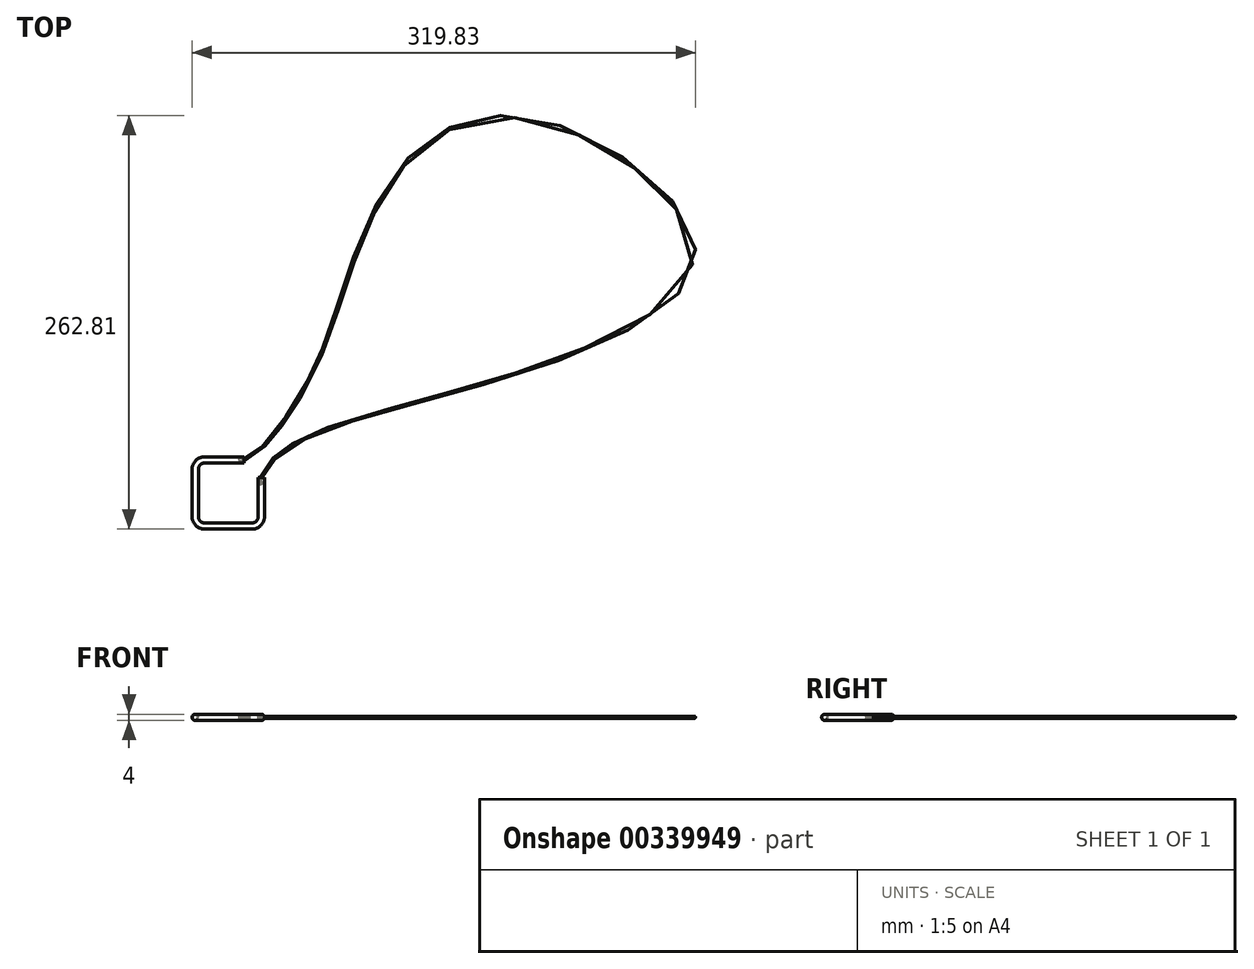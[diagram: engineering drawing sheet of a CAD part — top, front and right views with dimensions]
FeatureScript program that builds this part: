
annotation { "Feature Type Name" : "Feature", "Feature Type Description" : "" }
export const myFeature = defineFeature(function(context is Context, id is Id, definition is map)
    precondition{}
    {
        {
            var Q0;
            Q0=qCreatedBy(makeId("Top.planeOp"),FACE);
            var sketch = newSketch(context, id + "F0", { "sketchPlane" : qUnion([Q0])});
            skLineSegment(sketch, "E0.bottom", {"start": v(-23, 23) * mm, "end": v(23, 23) * mm});
            skLineSegment(sketch, "E0.top", {"start": v(-23, -23) * mm, "end": v(23, -23) * mm});
            skLineSegment(sketch, "E0.left", {"start": v(-23, 23) * mm, "end": v(-23, -23) * mm});
            skLineSegment(sketch, "E0.right", {"start": v(23, 23) * mm, "end": v(23, -23) * mm});
            skPoint(sketch, "E0.middle", {"position": v(0, 0) * mm});
            skSolve(sketch);
        }
        {
            var Q0;
            Q0 = qSketchRegion(id + "F0", true);
            extrude(context, id + "F1", {"entities" : qUnion([Q0]), "depth" : 2 * mm, "offsetDistance" : 25 * mm, "hasSecondDirection" : true, "secondDirectionOppositeDirection" : true, "secondDirectionDepth" : 2 * mm});
        }
        {
            var Q0;
            Q0=makeQuery(id+"F1.opExtrude","SWEPT_EDGE",EDGE,{"disambiguationData":[OSD([sQuery(id+"F0.wireOp",EDGE,"E0.bottom"),sQuery(id+"F0.wireOp",EDGE,"E0.left")])]});
            var Q1;
            Q1=makeQuery(id+"F1.opExtrude","SWEPT_EDGE",EDGE,{"disambiguationData":[OSD([sQuery(id+"F0.wireOp",EDGE,"E0.top"),sQuery(id+"F0.wireOp",EDGE,"E0.left")])]});
            var Q2;
            Q2=makeQuery(id+"F1.opExtrude","SWEPT_EDGE",EDGE,{"disambiguationData":[OSD([sQuery(id+"F0.wireOp",EDGE,"E0.top"),sQuery(id+"F0.wireOp",EDGE,"E0.right")])]});
            var Q3;
            Q3=makeQuery(id+"F1.opExtrude","SWEPT_EDGE",EDGE,{"disambiguationData":[OSD([sQuery(id+"F0.wireOp",EDGE,"E0.bottom"),sQuery(id+"F0.wireOp",EDGE,"E0.right")])]});
            fillet(context, id + "F2", {"entities" : qUnion([Q0, Q1, Q2, Q3]), "radius" : 8 * mm, "tangentPropagation" : true, "allowEdgeOverflow" : false});
        }
        {
            var Q0;
            Q0=makeQuery(id+"F1.opExtrude","CAP_FACE",FACE,{"disambiguationData":[OSD([sQuery(id+"F0.wireOp",EDGE,"E0.bottom"),sQuery(id+"F0.wireOp",EDGE,"E0.top"),sQuery(id+"F0.wireOp",EDGE,"E0.left"),sQuery(id+"F0.wireOp",EDGE,"E0.right")])],"isStart":false});
            var sketch = newSketch(context, id + "F3", { "sketchPlane" : qUnion([Q0])});
            skArc(sketch, "E1.0", {"start": v(-15, 19) * mm, "mid": v(-17.83, 17.83) * mm, "end": v(-19, 15) * mm});
            skLineSegment(sketch, "E1.1", {"start": v(15, 19) * mm, "end": v(-15, 19) * mm});
            skLineSegment(sketch, "E1.2", {"start": v(-19, 15) * mm, "end": v(-19, -15) * mm});
            skArc(sketch, "E1.3", {"start": v(19, 15) * mm, "mid": v(17.83, 17.83) * mm, "end": v(15, 19) * mm});
            skArc(sketch, "E1.4", {"start": v(-19, -15) * mm, "mid": v(-17.83, -17.83) * mm, "end": v(-15, -19) * mm});
            skLineSegment(sketch, "E1.5", {"start": v(-15, -19) * mm, "end": v(15, -19) * mm});
            skArc(sketch, "E1.6", {"start": v(15, -19) * mm, "mid": v(17.83, -17.83) * mm, "end": v(19, -15) * mm});
            skLineSegment(sketch, "E1.7", {"start": v(19, -15) * mm, "end": v(19, 15) * mm});
            skSolve(sketch);
        }
        {
            var Q0;
            Q0 = qSketchRegion(id + "F3", true);
            extrude(context, id + "F4", {"entities" : qUnion([Q0]), "operationType" : NewBodyOperationType.REMOVE, "oppositeDirection" : true, "depth" : 25 * mm, "offsetDistance" : 25 * mm});
        }
        {
            var Q0;
            Q0=makeQuery(id+"F1.opExtrude","CAP_FACE",FACE,{"disambiguationData":[OSD([sQuery(id+"F0.wireOp",EDGE,"E0.bottom"),sQuery(id+"F0.wireOp",EDGE,"E0.top"),sQuery(id+"F0.wireOp",EDGE,"E0.left"),sQuery(id+"F0.wireOp",EDGE,"E0.right")])],"isStart":false});
            var sketch = newSketch(context, id + "F5", { "sketchPlane" : qUnion([Q0])});
            skLineSegment(sketch, "E2", {"start": v(10, 23) * mm, "end": v(10, 19) * mm});
            skLineSegment(sketch, "E3", {"start": v(19, 10) * mm, "end": v(23, 10) * mm});
            skSolve(sketch);
        }
        {
            var Q0;
            {var subQ5=sQuery(id+"F5.wireOp",EDGE,"E2");Q0=makeQuery(id+"F5.imprint","IMPRINT",FACE,{"disambiguationData":[TD([[makeQuery(id+"F5.imprint","IMPRINT",EDGE,{"derivedFrom":subQ5}),1.0]])]});}
            extrude(context, id + "F6", {"entities" : qUnion([Q0]), "operationType" : NewBodyOperationType.REMOVE, "oppositeDirection" : true, "depth" : 25 * mm, "offsetDistance" : 25 * mm});
        }
        {
            var Q0;
            Q0=makeQuery(id+"F4.boolean.opBoolean","INTERSECT",EDGE,{"derivedFrom":[makeQuery(id+"F1.opExtrude","CAP_FACE",FACE,{"disambiguationData":[OSD([sQuery(id+"F0.wireOp",EDGE,"E0.bottom"),sQuery(id+"F0.wireOp",EDGE,"E0.top"),sQuery(id+"F0.wireOp",EDGE,"E0.left"),sQuery(id+"F0.wireOp",EDGE,"E0.right")])],"isStart":true}),makeQuery(id+"F4.opExtrude","SWEPT_FACE",FACE,{"disambiguationData":[OSD([sQuery(id+"F3.wireOp",EDGE,"E1.1")])]})]});
            var Q1;
            Q1=makeQuery(id+"F1.opExtrude","CAP_EDGE",EDGE,{"disambiguationData":[OSD([sQuery(id+"F0.wireOp",EDGE,"E0.bottom")])],"isStart":false});
            var Q2;
            Q2=makeQuery(id+"F4.boolean.opBoolean","COPY",EDGE,{"derivedFrom":makeQuery(id+"F4.opExtrude","CAP_EDGE",EDGE,{"disambiguationData":[OSD([sQuery(id+"F3.wireOp",EDGE,"E1.1")])],"isStart":true})});
            var Q3;
            Q3=makeQuery(id+"F1.opExtrude","CAP_EDGE",EDGE,{"disambiguationData":[OSD([sQuery(id+"F0.wireOp",EDGE,"E0.bottom")])],"isStart":true});
            fillet(context, id + "F7", {"entities" : qUnion([Q0, Q1, Q2, Q3]), "radius" : 2 * mm, "tangentPropagation" : true, "allowEdgeOverflow" : false});
        }
        {
            var Q0;
            Q0=makeQuery(id+"F6.boolean.opBoolean","COPY",FACE,{"derivedFrom":makeQuery(id+"F6.opExtrude","SWEPT_FACE",FACE,{"disambiguationData":[OSD([sQuery(id+"F5.wireOp",EDGE,"E3")])]})});
            var Q1;
            Q1=makeQuery(id+"F6.boolean.opBoolean","COPY",FACE,{"derivedFrom":makeQuery(id+"F6.opExtrude","SWEPT_FACE",FACE,{"disambiguationData":[OSD([sQuery(id+"F5.wireOp",EDGE,"E2")])]})});
            shell(context, id + "F8", {"entities" : qUnion([Q0, Q1]), "thickness" : 0.5 * mm});
        }
        {
            var Q0;
            Q0=qCreatedBy(makeId("Top.planeOp"),FACE);
            var sketch = newSketch(context, id + "F9", { "sketchPlane" : qUnion([Q0])});
            skFitSpline(sketch, "E4", {"points": [v(6.72, 21.47) * mm, v(14.06, 22.17) * mm, v(44.47, 59.55) * mm, v(66.74, 109.13) * mm, v(110.76, 207.91) * mm, v(200.62, 235.85) * mm, v(296.2, 150.37) * mm, v(172.68, 72.63) * mm, v(41.77, 31.23) * mm, v(21.21, 11.08) * mm, v(20.93, 5.25) * mm], "startDerivative": vector(191.17, -41.32) * mm, "endDerivative": vector(25.62, -173.75) * mm});
            skSolve(sketch);
        }
        {
            var Q0;
            Q0=sQuery(id+"F9.wireOp",EDGE,"E4");
            var Q1;
            Q1=sQuery(id+"F9.wireOp",VERTEX,"E4.end");
            cPlane(context, id + "F10", {"entities" : qUnion([Q0, Q1]), "cplaneType" : CPlaneType.CURVE_POINT, "offset" : 25 * mm, "width" : 150 * mm, "height" : 150 * mm});
        }
        {
            var Q0;
            Q0=qCreatedBy(id+"F10.planeOp",FACE);
            var sketch = newSketch(context, id + "F11", { "sketchPlane" : qUnion([Q0])});
            skPoint(sketch, "E5.0", {"position": v(21.48, 0) * mm});
            skCircle(sketch, "E6", {"center": v(21.48, 0) * mm, "radius": 0.6 * mm});
            skSolve(sketch);
        }
        {
            var Q0;
            Q0=makeQuery(id+"F11.imprint","IMPRINT",FACE,{"disambiguationData":[TD([[makeQuery(id+"F11.imprint","IMPRINT",EDGE,{"derivedFrom":sQuery(id+"F11.wireOp",EDGE,"E6")}),1.0]])]});
            var Q1;
            Q1=sQuery(id+"F9.wireOp",EDGE,"E4");
            sweep(context, id + "F12", {"profiles" : qUnion([Q0]), "path" : qUnion([Q1])});
        }
    });
